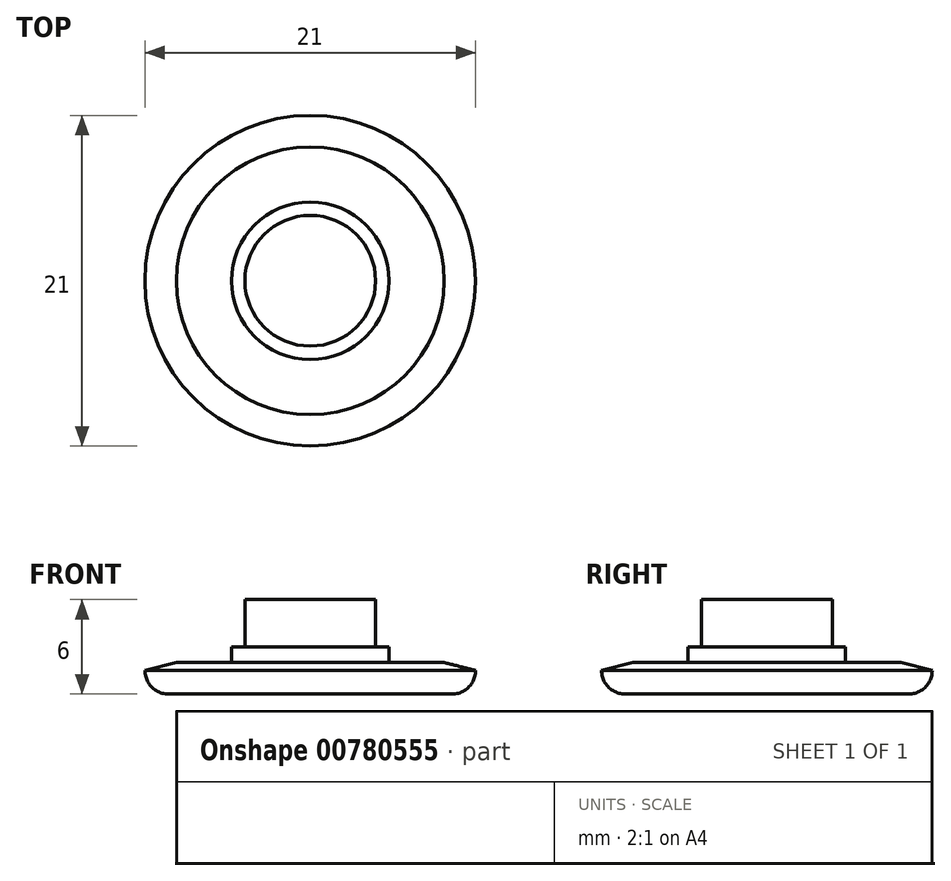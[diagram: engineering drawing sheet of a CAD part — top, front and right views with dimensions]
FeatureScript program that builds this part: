
annotation { "Feature Type Name" : "Feature", "Feature Type Description" : "" }
export const myFeature = defineFeature(function(context is Context, id is Id, definition is map)
    precondition{}
    {
        {
            var Q0;
            Q0=qCreatedBy(makeId("Top.planeOp"),FACE);
            var sketch = newSketch(context, id + "F0", { "sketchPlane" : qUnion([Q0])});
            skCircle(sketch, "E0", {"center": v(0, 0) * mm, "radius": 10.5 * mm});
            skSolve(sketch);
        }
        {
            var Q0;
            Q0=qSketchRegion(id+"F0",true);
            extrude(context, id + "F1", {"entities" : qUnion([Q0]), "depth" : 2 * mm, "offsetDistance" : 25 * mm});
        }
        {
            var Q0;
            Q0=makeQuery(id+"F1.opExtrude","CAP_FACE",FACE,{"disambiguationData":[OSD([sQuery(id+"F0.wireOp",EDGE,"E0")])],"isStart":false});
            var sketch = newSketch(context, id + "F2", { "sketchPlane" : qUnion([Q0])});
            skCircle(sketch, "E1", {"center": v(0, 0) * mm, "radius": 5 * mm});
            skSolve(sketch);
        }
        {
            var Q0;
            Q0=qSketchRegion(id+"F2",true);
            extrude(context, id + "F3", {"entities" : qUnion([Q0]), "operationType" : NewBodyOperationType.ADD, "depth" : 1 * mm, "offsetDistance" : 25 * mm});
        }
        {
            var Q0;
            Q0=makeQuery(id+"F3.opExtrude","CAP_FACE",FACE,{"disambiguationData":[OSD([sQuery(id+"F2.wireOp",EDGE,"E1")])],"isStart":false});
            var sketch = newSketch(context, id + "F4", { "sketchPlane" : qUnion([Q0])});
            skCircle(sketch, "E2", {"center": v(0, 0) * mm, "radius": 4.15 * mm});
            skSolve(sketch);
        }
        {
            var Q0;
            Q0=qSketchRegion(id+"F4",true);
            extrude(context, id + "F5", {"entities" : qUnion([Q0]), "operationType" : NewBodyOperationType.ADD, "depth" : 3 * mm, "offsetDistance" : 25 * mm});
        }
        {
            var Q0;
            Q0=makeQuery(id+"F1.opExtrude","CAP_EDGE",EDGE,{"disambiguationData":[OSD([sQuery(id+"F0.wireOp",EDGE,"E0")])],"isStart":false});
            chamfer(context, id + "F6", {"entities" : qUnion([Q0]), "chamferType" : ChamferType.TWO_OFFSETS, "width1" : 2 * mm, "oppositeDirection" : false, "width2" : .5 * mm, "tangentPropagation" : true});
        }
        {
            var Q0;
            Q0=makeQuery(id+"F1.opExtrude","CAP_EDGE",EDGE,{"disambiguationData":[OSD([sQuery(id+"F0.wireOp",EDGE,"E0")])],"isStart":true});
            fillet(context, id + "F7", {"entities" : qUnion([Q0]), "radius" : 1.5 * mm, "tangentPropagation" : true, "allowEdgeOverflow" : false});
        }
    });
